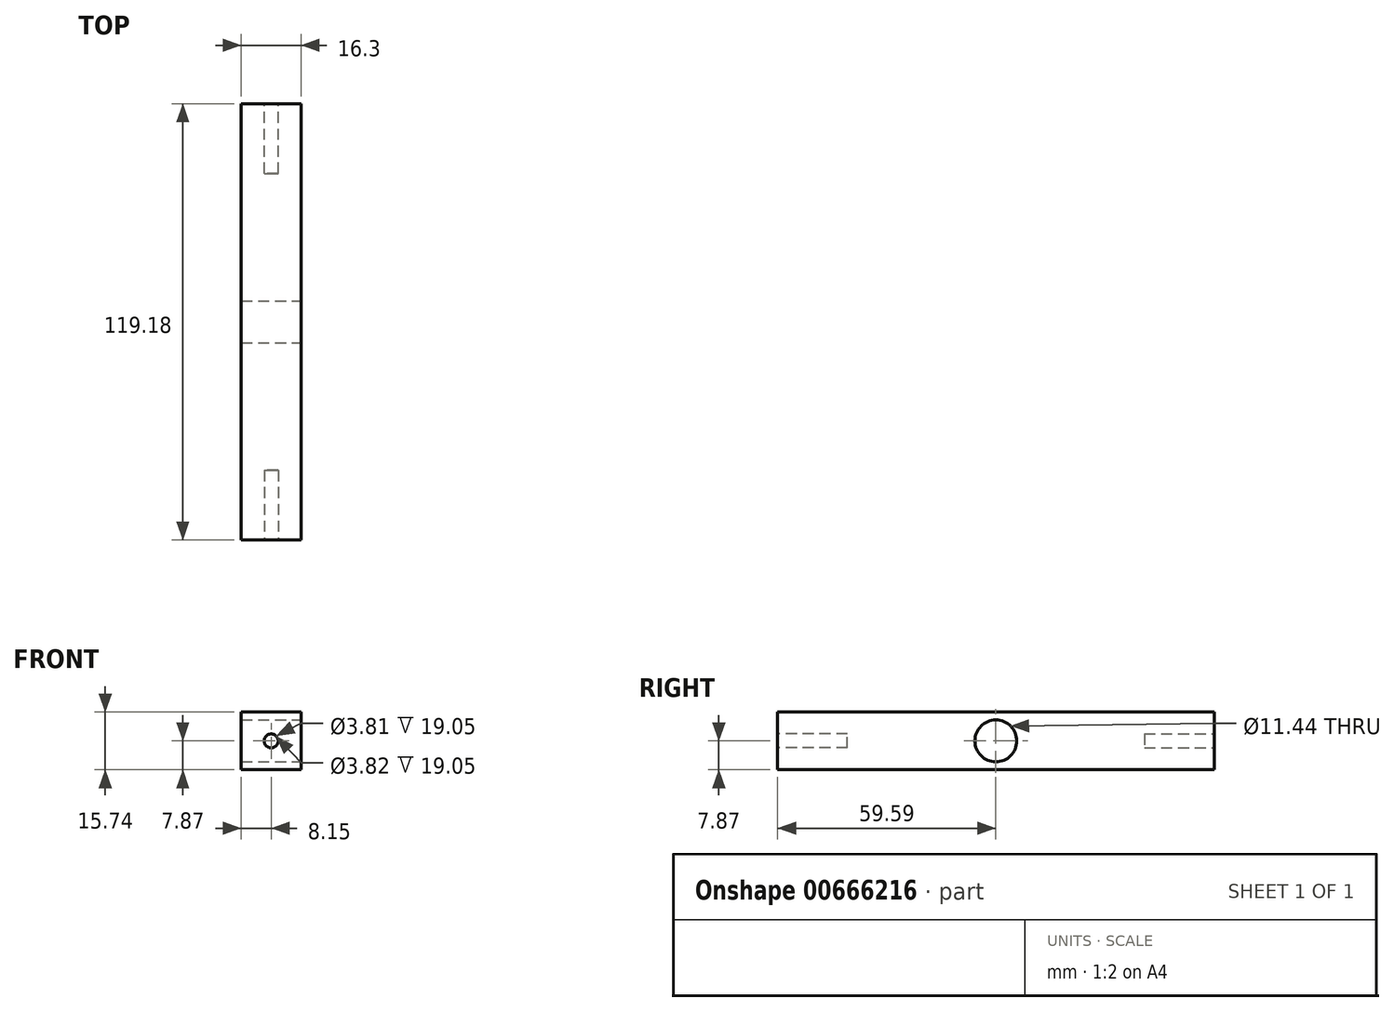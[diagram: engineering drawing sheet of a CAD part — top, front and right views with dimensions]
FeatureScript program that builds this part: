
annotation { "Feature Type Name" : "Feature", "Feature Type Description" : "" }
export const myFeature = defineFeature(function(context is Context, id is Id, definition is map)
    precondition{}
    {
        {
            var Q0;
            Q0=qCreatedBy(makeId("Front.planeOp"),FACE);
            var sketch = newSketch(context, id + "F0", { "sketchPlane" : qUnion([Q0])});
            skLineSegment(sketch, "E0.bottom", {"start": v(8.15, -7.87) * mm, "end": v(-8.15, -7.87) * mm});
            skLineSegment(sketch, "E0.top", {"start": v(8.15, 7.87) * mm, "end": v(-8.15, 7.87) * mm});
            skLineSegment(sketch, "E0.left", {"start": v(8.15, -7.87) * mm, "end": v(8.15, 7.87) * mm});
            skLineSegment(sketch, "E0.right", {"start": v(-8.15, -7.87) * mm, "end": v(-8.15, 7.87) * mm});
            skPoint(sketch, "E0.middle", {"position": v(0, 0) * mm});
            skSolve(sketch);
        }
        {
            var Q0;
            Q0=makeQuery(id+"F0.imprint","IMPRINT",FACE,{"disambiguationData":[TD([[makeQuery(id+"F0.imprint","IMPRINT",EDGE,{"derivedFrom":sQuery(id+"F0.wireOp",EDGE,"E0.bottom")}),-1.0]])]});
            extrude(context, id + "F1", {"entities" : qUnion([Q0]), "depth" : 59.6 * mm, "offsetDistance" : 25.4 * mm, "hasSecondDirection" : true, "secondDirectionOppositeDirection" : true, "secondDirectionDepth" : 59.6 * mm});
        }
        {
            var Q0;
            Q0=makeQuery(id+"F1.opExtrude","SWEPT_FACE",FACE,{"disambiguationData":[OSD([sQuery(id+"F0.wireOp",EDGE,"E0.left")])]});
            var sketch = newSketch(context, id + "F2", { "sketchPlane" : qUnion([Q0])});
            skCircle(sketch, "E1", {"center": v(0, 0) * mm, "radius": 5.72 * mm});
            skSolve(sketch);
        }
        {
            var Q0;
            Q0=makeQuery(id+"F2.imprint","IMPRINT",FACE,{"disambiguationData":[TD([[makeQuery(id+"F2.imprint","IMPRINT",EDGE,{"derivedFrom":sQuery(id+"F2.wireOp",EDGE,"E1")}),1.0]])]});
            extrude(context, id + "F3", {"entities" : qUnion([Q0]), "operationType" : NewBodyOperationType.REMOVE, "oppositeDirection" : true, "depth" : 18.54 * mm, "offsetDistance" : 25.4 * mm});
        }
        {
            var Q0;
            Q0=makeQuery(id+"F1.opExtrude","CAP_FACE",FACE,{"disambiguationData":[OSD([sQuery(id+"F0.wireOp",EDGE,"E0.bottom"),sQuery(id+"F0.wireOp",EDGE,"E0.top"),sQuery(id+"F0.wireOp",EDGE,"E0.left"),sQuery(id+"F0.wireOp",EDGE,"E0.right")])],"isStart":false});
            var sketch = newSketch(context, id + "F4", { "sketchPlane" : qUnion([Q0])});
            skCircle(sketch, "E2", {"center": v(0, 0) * mm, "radius": 1.9 * mm});
            skSolve(sketch);
        }
        {
            var Q0;
            Q0=makeQuery(id+"F4.imprint","IMPRINT",FACE,{"disambiguationData":[TD([[makeQuery(id+"F4.imprint","IMPRINT",EDGE,{"derivedFrom":sQuery(id+"F4.wireOp",EDGE,"E2")}),1.0]])]});
            extrude(context, id + "F5", {"entities" : qUnion([Q0]), "operationType" : NewBodyOperationType.REMOVE, "oppositeDirection" : true, "depth" : 19.05 * mm, "offsetDistance" : 25.4 * mm});
        }
        {
            var Q0;
            Q0=makeQuery(id+"F1.opExtrude","CAP_FACE",FACE,{"disambiguationData":[OSD([sQuery(id+"F0.wireOp",EDGE,"E0.bottom"),sQuery(id+"F0.wireOp",EDGE,"E0.top"),sQuery(id+"F0.wireOp",EDGE,"E0.left"),sQuery(id+"F0.wireOp",EDGE,"E0.right")])],"isStart":true});
            var sketch = newSketch(context, id + "F6", { "sketchPlane" : qUnion([Q0])});
            skCircle(sketch, "E3", {"center": v(0, 0) * mm, "radius": 1.9 * mm});
            skSolve(sketch);
        }
        {
            var Q0;
            Q0=makeQuery(id+"F6.imprint","IMPRINT",FACE,{"disambiguationData":[TD([[makeQuery(id+"F6.imprint","IMPRINT",EDGE,{"derivedFrom":sQuery(id+"F6.wireOp",EDGE,"E3")}),1.0]])]});
            extrude(context, id + "F7", {"entities" : qUnion([Q0]), "operationType" : NewBodyOperationType.REMOVE, "oppositeDirection" : true, "depth" : 19.05 * mm, "offsetDistance" : 25.4 * mm});
        }
    });
